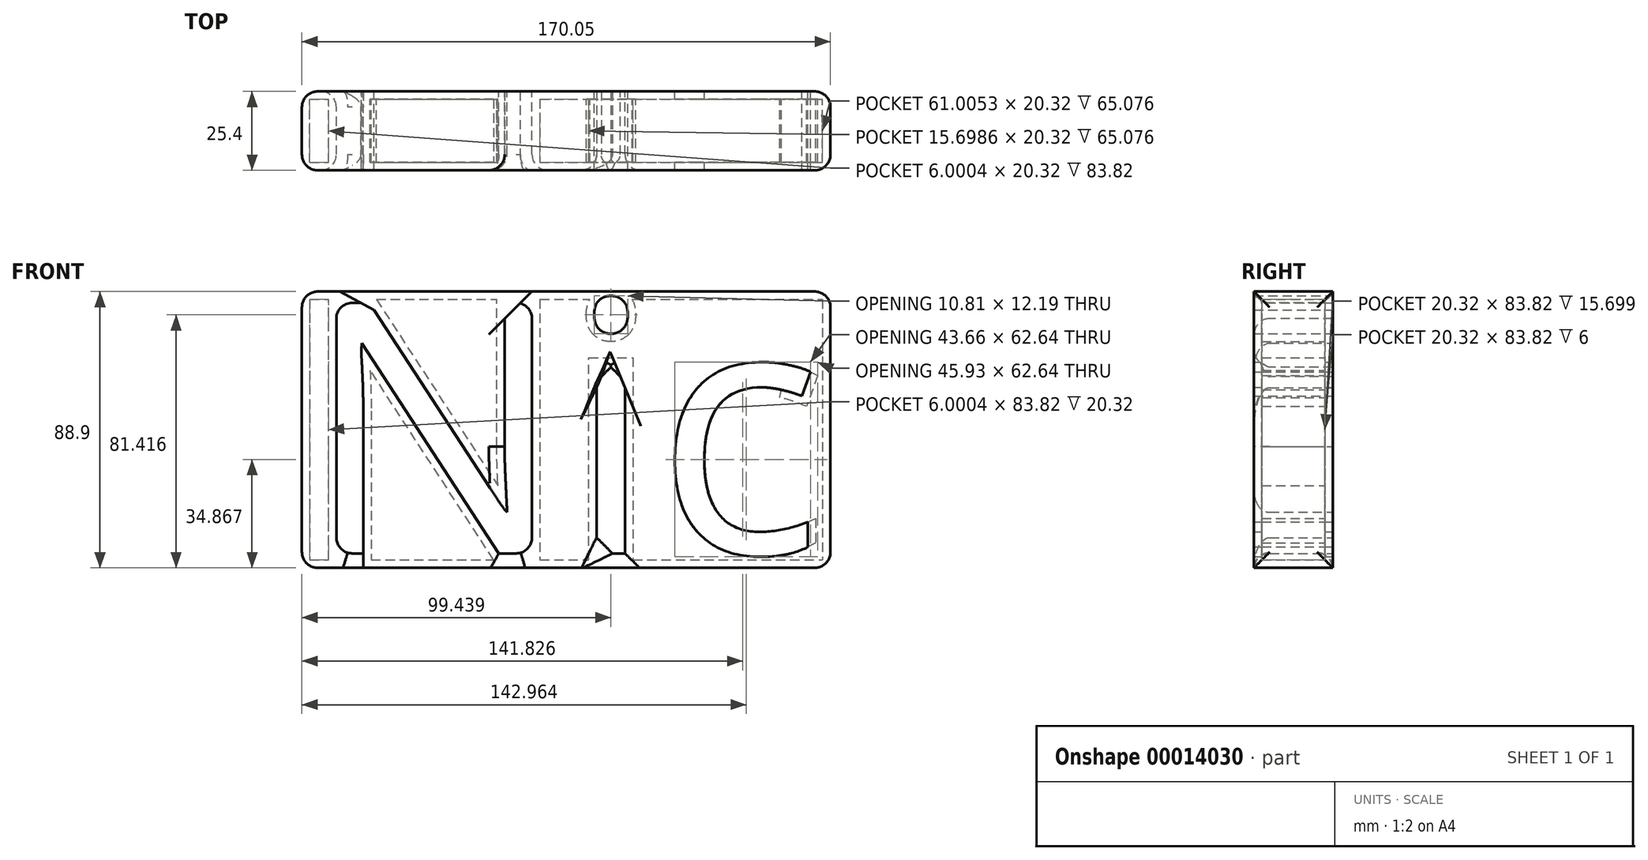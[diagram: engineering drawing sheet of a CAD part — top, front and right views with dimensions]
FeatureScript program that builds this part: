
annotation { "Feature Type Name" : "Feature", "Feature Type Description" : "" }
export const myFeature = defineFeature(function(context is Context, id is Id, definition is map)
    precondition{}
    {
        {
            var Q0;
            Q0=qCreatedBy(makeId("Front.planeOp"),FACE);
            var sketch = newSketch(context, id + "F0", { "sketchPlane" : qUnion([Q0])});
            skText(sketch, "E0", { "text": "Nic", "fontName": "OpenSans-Regular.ttf"});
            skLineSegment(sketch, "E1.bottom", {"start": v(-76.73, 46.54) * mm, "end": v(93.32, 46.54) * mm});
            skLineSegment(sketch, "E1.top", {"start": v(-76.73, -42.36) * mm, "end": v(93.32, -42.36) * mm});
            skLineSegment(sketch, "E1.left", {"start": v(-76.73, 46.54) * mm, "end": v(-76.73, -42.36) * mm});
            skLineSegment(sketch, "E1.right", {"start": v(93.32, 46.54) * mm, "end": v(93.32, -42.36) * mm});
            const initialGuessF0  = {"E0": [-0.07673, -0.0377, 1, 0, 0.08128]};
            skSetInitialGuess(sketch, initialGuessF0);
            skSolve(sketch);
        }
        {
            var Q0;
            Q0=makeQuery(id+"F0.imprint","IMPRINT",FACE,{"disambiguationData":[TD([[makeQuery(id+"F0.imprint","IMPRINT",EDGE,{"derivedFrom":sQuery(id+"F0.wireOp",EDGE,"E0.sketch_text.stroke-0")}),1.0]])]});
            extrude(context, id + "F1", {"entities" : qUnion([Q0]), "depth" : 25.4 * mm});
        }
        {
            var Q0;
            Q0=makeQuery(id+"F1.opExtrude","SWEPT_FACE",FACE,{"disambiguationData":[OSD([sQuery(id+"F0.wireOp",EDGE,"E0.sketch_text.stroke-37")])]});
            var Q1;
            Q1=makeQuery(id+"F1.opExtrude","SWEPT_FACE",FACE,{"disambiguationData":[OSD([sQuery(id+"F0.wireOp",EDGE,"E0.sketch_text.stroke-39")])]});
            var Q2;
            Q2=makeQuery(id+"F1.opExtrude","SWEPT_FACE",FACE,{"disambiguationData":[OSD([sQuery(id+"F0.wireOp",EDGE,"E0.sketch_text.stroke-27")])]});
            var Q3;
            Q3=makeQuery(id+"F1.opExtrude","SWEPT_FACE",FACE,{"disambiguationData":[OSD([sQuery(id+"F0.wireOp",EDGE,"E0.sketch_text.stroke-31")])]});
            var Q4;
            Q4=makeQuery(id+"F1.opExtrude","SWEPT_FACE",FACE,{"disambiguationData":[OSD([sQuery(id+"F0.wireOp",EDGE,"E0.sketch_text.stroke-38")])]});
            var Q5;
            Q5=makeQuery(id+"F1.opExtrude","SWEPT_FACE",FACE,{"disambiguationData":[OSD([sQuery(id+"F0.wireOp",EDGE,"E0.sketch_text.stroke-29")])]});
            var Q6;
            Q6=makeQuery(id+"F1.opExtrude","SWEPT_FACE",FACE,{"disambiguationData":[OSD([sQuery(id+"F0.wireOp",EDGE,"E0.sketch_text.stroke-30")])]});
            var Q7;
            Q7=makeQuery(id+"F1.opExtrude","SWEPT_FACE",FACE,{"disambiguationData":[OSD([sQuery(id+"F0.wireOp",EDGE,"E0.sketch_text.stroke-36")])]});
            var Q8;
            Q8=makeQuery(id+"F1.opExtrude","SWEPT_FACE",FACE,{"disambiguationData":[OSD([sQuery(id+"F0.wireOp",EDGE,"E0.sketch_text.stroke-28")])]});
            var Q9;
            Q9=makeQuery(id+"F1.opExtrude","SWEPT_FACE",FACE,{"disambiguationData":[OSD([sQuery(id+"F0.wireOp",EDGE,"E0.sketch_text.stroke-41")])]});
            var Q10;
            Q10=makeQuery(id+"F1.opExtrude","SWEPT_FACE",FACE,{"disambiguationData":[OSD([sQuery(id+"F0.wireOp",EDGE,"E0.sketch_text.stroke-32")])]});
            var Q11;
            Q11=makeQuery(id+"F1.opExtrude","SWEPT_FACE",FACE,{"disambiguationData":[OSD([sQuery(id+"F0.wireOp",EDGE,"E0.sketch_text.stroke-35")])]});
            shell(context, id + "F2", {"entities" : qUnion([Q0, Q1, Q2, Q3, Q4, Q5, Q6, Q7, Q8, Q9, Q10, Q11]), "thickness" : 2.54 * mm});
        }
        {
            var Q0;
            Q0=makeQuery(id+"F1.opExtrude","SWEPT_EDGE",EDGE,{"disambiguationData":[OSD([sQuery(id+"F0.wireOp",EDGE,"E0.sketch_text.stroke-5"),sQuery(id+"F0.wireOp",EDGE,"E0.sketch_text.stroke-6")])]});
            fillet(context, id + "F3", {"entities" : qUnion([Q0]), "radius" : 5.08 * mm, "tangentPropagation" : true, "allowEdgeOverflow" : false});
        }
        {
            var Q0;
            Q0=makeQuery(id+"F1.opExtrude","CAP_EDGE",EDGE,{"disambiguationData":[OSD([sQuery(id+"F0.wireOp",EDGE,"E0.sketch_text.stroke-16")])],"isStart":false});
            var Q1;
            Q1=makeQuery(id+"F1.opExtrude","CAP_EDGE",EDGE,{"disambiguationData":[OSD([sQuery(id+"F0.wireOp",EDGE,"E0.sketch_text.stroke-17")])],"isStart":false});
            var Q2;
            Q2=makeQuery(id+"F1.opExtrude","CAP_EDGE",EDGE,{"disambiguationData":[OSD([sQuery(id+"F0.wireOp",EDGE,"E0.sketch_text.stroke-15")])],"isStart":false});
            var Q3;
            Q3=makeQuery(id+"F1.opExtrude","CAP_EDGE",EDGE,{"disambiguationData":[OSD([sQuery(id+"F0.wireOp",EDGE,"E0.sketch_text.stroke-18")])],"isStart":false});
            fillet(context, id + "F4", {"entities" : qUnion([Q0, Q1, Q2, Q3]), "radius" : 5.08 * mm, "tangentPropagation" : true, "allowEdgeOverflow" : false});
        }
        {
            var Q0;
            Q0=makeQuery(id+"F1.opExtrude","SWEPT_EDGE",EDGE,{"disambiguationData":[OSD([sQuery(id+"F0.wireOp",EDGE,"E0.sketch_text.stroke-0"),sQuery(id+"F0.wireOp",EDGE,"E0.sketch_text.stroke-14")])]});
            var Q1;
            Q1=makeQuery(id+"F1.opExtrude","SWEPT_EDGE",EDGE,{"disambiguationData":[OSD([sQuery(id+"F0.wireOp",EDGE,"E0.sketch_text.stroke-6"),sQuery(id+"F0.wireOp",EDGE,"E0.sketch_text.stroke-7")])]});
            var Q2;
            Q2=makeQuery(id+"F1.opExtrude","SWEPT_EDGE",EDGE,{"disambiguationData":[OSD([sQuery(id+"F0.wireOp",EDGE,"E0.sketch_text.stroke-13"),sQuery(id+"F0.wireOp",EDGE,"E0.sketch_text.stroke-14")])]});
            fillet(context, id + "F5", {"entities" : qUnion([Q0, Q1, Q2]), "radius" : 5.08 * mm, "tangentPropagation" : true, "allowEdgeOverflow" : false});
        }
        {
            var Q0;
            Q0=makeQuery(id+"F1.opExtrude","SWEPT_EDGE",EDGE,{"disambiguationData":[OSD([sQuery(id+"F0.wireOp",EDGE,"E0.sketch_text.stroke-16"),sQuery(id+"F0.wireOp",EDGE,"E0.sketch_text.stroke-17")])]});
            chamfer(context, id + "F6", {"entities" : qUnion([Q0]), "width" : 5.08 * mm, "tangentPropagation" : true});
        }
        {
            var Q0;
            Q0=makeQuery(id+"F1.opExtrude","SWEPT_EDGE",EDGE,{"disambiguationData":[OSD([sQuery(id+"F0.wireOp",EDGE,"E0.sketch_text.stroke-17"),sQuery(id+"F0.wireOp",EDGE,"E0.sketch_text.stroke-18")])]});
            chamfer(context, id + "F7", {"entities" : qUnion([Q0]), "width" : 5.08 * mm, "tangentPropagation" : true});
        }
        {
            var Q0;
            {var subQ0=sQuery(id+"F0.wireOp",EDGE,"E0.sketch_text.stroke-16");Q0=makeQuery(id+"F6.opChamfer","BLEND_EDGE",EDGE,{"blendedFrom":[makeQuery(id+"F1.opExtrude","SWEPT_EDGE",EDGE,{"disambiguationData":[OSD([subQ0,sQuery(id+"F0.wireOp",EDGE,"E0.sketch_text.stroke-17")])]}),makeQuery(id+"F1.opExtrude","SWEPT_FACE",FACE,{"disambiguationData":[OSD([subQ0])]})],"blendedInto":[makeQuery(id+"F1.opExtrude","SWEPT_FACE",FACE,{"disambiguationData":[OSD([subQ0])]})]});}
            var Q1;
            {var subQ0=sQuery(id+"F0.wireOp",EDGE,"E0.sketch_text.stroke-18");Q1=makeQuery(id+"F7.opChamfer","BLEND_EDGE",EDGE,{"blendedFrom":[makeQuery(id+"F1.opExtrude","SWEPT_EDGE",EDGE,{"disambiguationData":[OSD([sQuery(id+"F0.wireOp",EDGE,"E0.sketch_text.stroke-17"),subQ0])]}),makeQuery(id+"F1.opExtrude","SWEPT_FACE",FACE,{"disambiguationData":[OSD([subQ0])]})],"blendedInto":[makeQuery(id+"F1.opExtrude","SWEPT_FACE",FACE,{"disambiguationData":[OSD([subQ0])]})]});}
            var Q2;
            Q2=makeQuery(id+"F1.opExtrude","SWEPT_EDGE",EDGE,{"disambiguationData":[OSD([sQuery(id+"F0.wireOp",EDGE,"E0.sketch_text.stroke-15"),sQuery(id+"F0.wireOp",EDGE,"E0.sketch_text.stroke-16")])]});
            chamfer(context, id + "F8", {"entities" : qUnion([Q0, Q1, Q2]), "width" : 5.08 * mm, "tangentPropagation" : true});
        }
        {
            var Q0;
            Q0=makeQuery(id+"F1.opExtrude","SWEPT_EDGE",EDGE,{"disambiguationData":[OSD([sQuery(id+"F0.wireOp",EDGE,"E0.sketch_text.stroke-12"),sQuery(id+"F0.wireOp",EDGE,"E0.sketch_text.stroke-13")])]});
            chamfer(context, id + "F9", {"entities" : qUnion([Q0]), "width" : 5.08 * mm, "tangentPropagation" : true});
        }
        {
            var Q0;
            Q0=makeQuery(id+"F1.opExtrude","SWEPT_EDGE",EDGE,{"disambiguationData":[OSD([sQuery(id+"F0.wireOp",EDGE,"E0.sketch_text.stroke-7"),sQuery(id+"F0.wireOp",EDGE,"E0.sketch_text.stroke-8")])]});
            chamfer(context, id + "F10", {"entities" : qUnion([Q0]), "width" : 5.08 * mm, "tangentPropagation" : true});
        }
        {
            var Q0;
            Q0=makeQuery(id+"F1.opExtrude","SWEPT_FACE",FACE,{"disambiguationData":[OSD([sQuery(id+"F0.wireOp",EDGE,"E1.right")])]});
            fillet(context, id + "F11", {"entities" : qUnion([Q0]), "radius" : 5.08 * mm, "allowEdgeOverflow" : false});
        }
        {
            var Q0;
            Q0=makeQuery(id+"FIG3KdmWkhYhfhr_1.opChamfer","BLEND_FACE",FACE,{"disambiguationData":[OSD([sQuery(id+"F0.wireOp",EDGE,"E0.sketch_text.stroke-4"),sQuery(id+"F0.wireOp",EDGE,"E0.sketch_text.stroke-5")])]});
            var Q1;
            Q1=makeQuery(id+"F3.opFillet","BLEND_FACE",FACE,{"disambiguationData":[OSD([sQuery(id+"F0.wireOp",EDGE,"E0.sketch_text.stroke-5"),sQuery(id+"F0.wireOp",EDGE,"E0.sketch_text.stroke-6")])]});
            var Q2;
            Q2=makeQuery(id+"FIG3KdmWkhYhfhr_1.opChamfer","BLEND_EDGE",EDGE,{"blendedFrom":[makeQuery(id+"F1.opExtrude","SWEPT_EDGE",EDGE,{"disambiguationData":[OSD([sQuery(id+"F0.wireOp",EDGE,"E0.sketch_text.stroke-2"),sQuery(id+"F0.wireOp",EDGE,"E0.sketch_text.stroke-3")])]}),makeQuery(id+"F1.opExtrude","SWEPT_FACE",FACE,{"disambiguationData":[OSD([sQuery(id+"F0.wireOp",EDGE,"E0.sketch_text.stroke-1")])]})],"blendedInto":[makeQuery(id+"F1.opExtrude","SWEPT_FACE",FACE,{"disambiguationData":[OSD([sQuery(id+"F0.wireOp",EDGE,"E0.sketch_text.stroke-1")])]})]});
            var Q3;
            Q3=makeQuery(id+"FIG3KdmWkhYhfhr_1.opChamfer","BLEND_FACE",FACE,{"disambiguationData":[OSD([sQuery(id+"F0.wireOp",EDGE,"E0.sketch_text.stroke-2"),sQuery(id+"F0.wireOp",EDGE,"E0.sketch_text.stroke-3")])]});
            fillet(context, id + "F12", {"entities" : qUnion([Q0, Q1, Q2, Q3]), "radius" : 5.08 * mm, "tangentPropagation" : true, "allowEdgeOverflow" : false});
        }
        {
            var Q0;
            Q0=makeQuery(id+"F1.opExtrude","SWEPT_EDGE",EDGE,{"disambiguationData":[OSD([sQuery(id+"F0.wireOp",EDGE,"E0.sketch_text.stroke-2"),sQuery(id+"F0.wireOp",EDGE,"E0.sketch_text.stroke-3")])]});
            fillet(context, id + "F13", {"entities" : qUnion([Q0]), "radius" : 25.4 * mm, "tangentPropagation" : true, "allowEdgeOverflow" : false});
        }
        {
            var Q0;
            Q0=makeQuery(id+"F1.opExtrude","CAP_EDGE",EDGE,{"disambiguationData":[OSD([sQuery(id+"F0.wireOp",EDGE,"E0.sketch_text.stroke-14")])],"isStart":false});
            fillet(context, id + "F14", {"entities" : qUnion([Q0]), "radius" : 5.08 * mm, "tangentPropagation" : true, "allowEdgeOverflow" : false});
        }
        {
            var Q0;
            Q0=makeQuery(id+"F1.opExtrude","CAP_EDGE",EDGE,{"disambiguationData":[OSD([sQuery(id+"F0.wireOp",EDGE,"E0.sketch_text.stroke-10")])],"isStart":false});
            var Q1;
            Q1=makeQuery(id+"F1.opExtrude","CAP_EDGE",EDGE,{"disambiguationData":[OSD([sQuery(id+"F0.wireOp",EDGE,"E0.sketch_text.stroke-12")])],"isStart":false});
            var Q2;
            Q2=makeQuery(id+"F1.opExtrude","CAP_EDGE",EDGE,{"disambiguationData":[OSD([sQuery(id+"F0.wireOp",EDGE,"E0.sketch_text.stroke-11")])],"isStart":false});
            fillet(context, id + "F15", {"entities" : qUnion([Q0, Q1, Q2]), "radius" : 5.08 * mm, "tangentPropagation" : true, "allowEdgeOverflow" : false});
        }
        {
            var Q0;
            Q0=makeQuery(id+"F1.opExtrude","CAP_EDGE",EDGE,{"disambiguationData":[OSD([sQuery(id+"F0.wireOp",EDGE,"E0.sketch_text.stroke-1")])],"isStart":false});
            fillet(context, id + "F16", {"entities" : qUnion([Q0]), "radius" : 5.08 * mm, "tangentPropagation" : true, "allowEdgeOverflow" : false});
        }
        {
            var Q0;
            Q0=makeQuery(id+"F1.opExtrude","SWEPT_EDGE",EDGE,{"disambiguationData":[OSD([sQuery(id+"F0.wireOp",EDGE,"E0.sketch_text.stroke-8"),sQuery(id+"F0.wireOp",EDGE,"E0.sketch_text.stroke-9")])]});
            fillet(context, id + "F17", {"entities" : qUnion([Q0]), "radius" : 25.4 * mm, "tangentPropagation" : true, "allowEdgeOverflow" : false});
        }
        {
            var Q0;
            Q0=makeQuery(id+"F1.opExtrude","SWEPT_FACE",FACE,{"disambiguationData":[OSD([sQuery(id+"F0.wireOp",EDGE,"E1.left")])]});
            fillet(context, id + "F18", {"entities" : qUnion([Q0]), "radius" : 5.08 * mm, "tangentPropagation" : true, "allowEdgeOverflow" : false});
        }
    });
